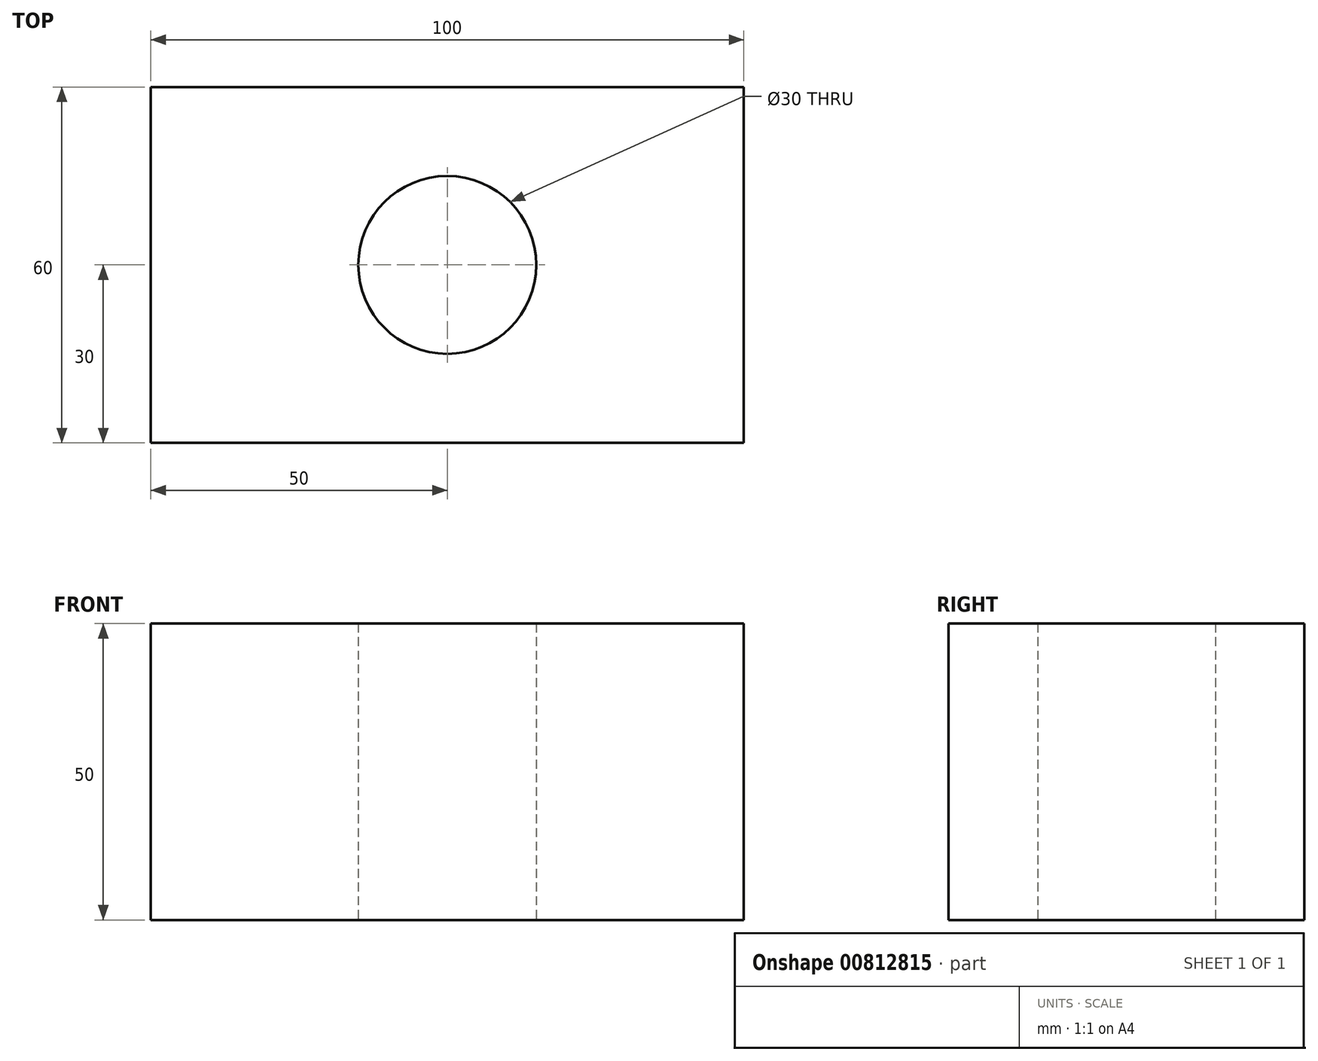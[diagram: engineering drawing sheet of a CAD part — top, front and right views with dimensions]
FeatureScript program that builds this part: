
annotation { "Feature Type Name" : "Feature", "Feature Type Description" : "" }
export const myFeature = defineFeature(function(context is Context, id is Id, definition is map)
    precondition{}
    {
        {
            var Q0;
            Q0=qCreatedBy(makeId("Top.planeOp"),FACE);
            var sketch = newSketch(context, id + "F0", { "sketchPlane" : qUnion([Q0])});
            skLineSegment(sketch, "E0.bottom", {"start": v(-50, 30) * mm, "end": v(50, 30) * mm});
            skLineSegment(sketch, "E0.top", {"start": v(-50, -30) * mm, "end": v(50, -30) * mm});
            skLineSegment(sketch, "E0.left", {"start": v(-50, 30) * mm, "end": v(-50, -30) * mm});
            skLineSegment(sketch, "E0.right", {"start": v(50, 30) * mm, "end": v(50, -30) * mm});
            skCircle(sketch, "E1", {"center": v(0, 0) * mm, "radius": 15 * mm});
            skSolve(sketch);
        }
        {
            var Q0;
            Q0=makeQuery(id+"F0.imprint","IMPRINT",FACE,{"disambiguationData":[TD([[makeQuery(id+"F0.imprint","IMPRINT",EDGE,{"derivedFrom":sQuery(id+"F0.wireOp",EDGE,"E0.bottom")}),-1.0]])]});
            extrude(context, id + "F1", {"entities" : qUnion([Q0]), "depth" : 50 * mm, "offsetDistance" : 25 * mm});
        }
    });
